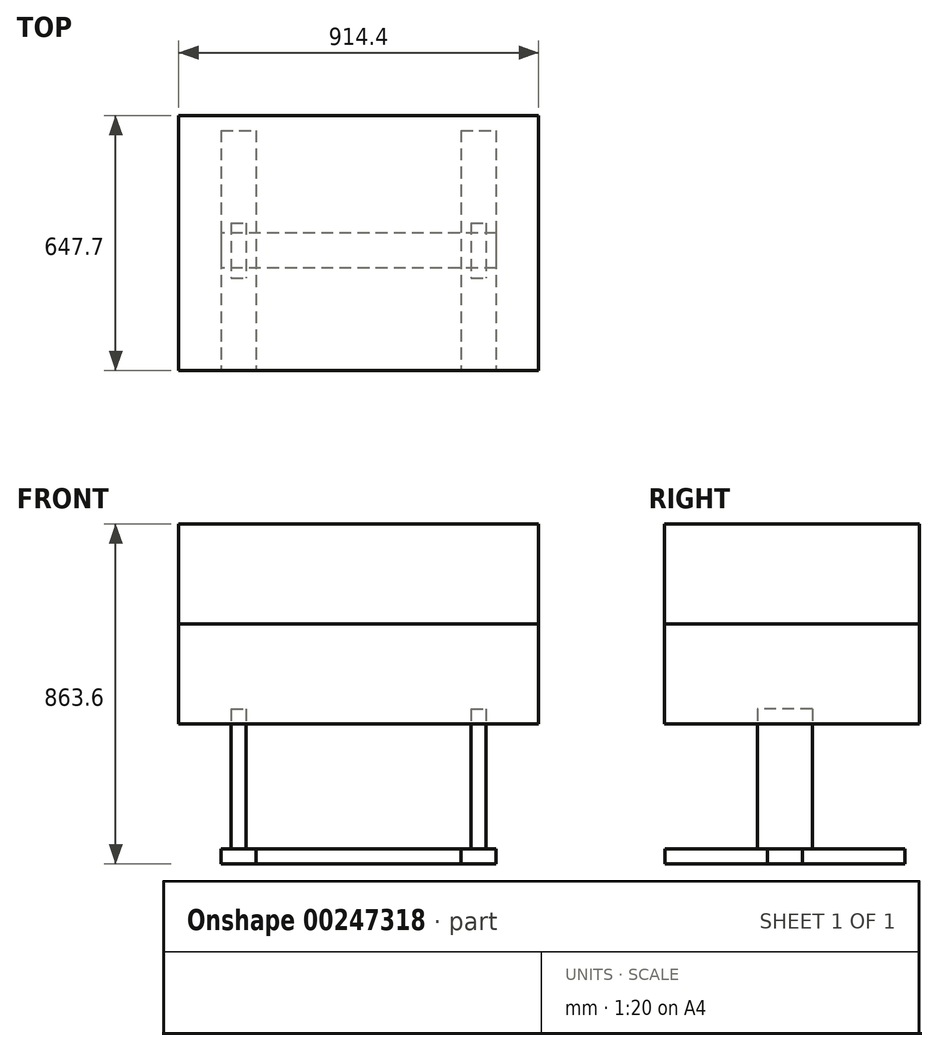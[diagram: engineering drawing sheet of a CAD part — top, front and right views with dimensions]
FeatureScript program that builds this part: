
annotation { "Feature Type Name" : "Feature", "Feature Type Description" : "" }
export const myFeature = defineFeature(function(context is Context, id is Id, definition is map)
    precondition{}
    {
        {
            var Q0;
            Q0=qCreatedBy(makeId("Top.planeOp"),FACE);
            var sketch = newSketch(context, id + "F0", { "sketchPlane" : qUnion([Q0])});
            skLineSegment(sketch, "E0.bottom", {"start": v(-85.28, 304.8) * mm, "end": v(3.62, 304.8) * mm});
            skLineSegment(sketch, "E0.top", {"start": v(-85.28, -304.8) * mm, "end": v(3.62, -304.8) * mm});
            skLineSegment(sketch, "E0.left", {"start": v(-85.28, 304.8) * mm, "end": v(-85.28, -304.8) * mm});
            skLineSegment(sketch, "E0.right", {"start": v(3.62, 304.8) * mm, "end": v(3.62, -304.8) * mm});
            skSolve(sketch);
        }
        {
            var Q0;
            Q0=makeQuery(id+"F0.imprint","IMPRINT",FACE,{"disambiguationData":[TD([[makeQuery(id+"F0.imprint","IMPRINT",EDGE,{"derivedFrom":sQuery(id+"F0.wireOp",EDGE,"E0.bottom")}),-1.0]])]});
            extrude(context, id + "F1", {"entities" : qUnion([Q0]), "depth" : 38.1 * mm});
        }
        {
            var Q0;
            Q0=makeQuery(id+"F1.opExtrude","SWEPT_BODY",BODY,{"disambiguationData":[OSD([sQuery(id+"F0.wireOp",EDGE,"E0.bottom"),sQuery(id+"F0.wireOp",EDGE,"E0.top"),sQuery(id+"F0.wireOp",EDGE,"E0.left"),sQuery(id+"F0.wireOp",EDGE,"E0.right")])]});
            transform(context, id + "F2", {"entities" : qUnion([Q0]), "transformType" : TransformType.TRANSLATION_3D, "dx" : 609.6 * mm, "dy" : 0 * mm, "dz" : 0 * mm, "makeCopy" : true});
        }
        {
            var Q0;
            Q0=makeQuery(id+"F2.opPattern","COPY",FACE,{"derivedFrom":makeQuery(id+"F1.opExtrude","SWEPT_FACE",FACE,{"disambiguationData":[OSD([sQuery(id+"F0.wireOp",EDGE,"E0.bottom")])]}),"instanceName":"1"});
            var sketch = newSketch(context, id + "F3", { "sketchPlane" : qUnion([Q0])});
            skLineSegment(sketch, "E1.bottom", {"start": v(-613.22, 38.1) * mm, "end": v(85.28, 38.1) * mm});
            skLineSegment(sketch, "E1.top", {"start": v(-613.22, 0) * mm, "end": v(85.28, 0) * mm});
            skLineSegment(sketch, "E1.left", {"start": v(-613.22, 38.1) * mm, "end": v(-613.22, 0) * mm});
            skLineSegment(sketch, "E1.right", {"start": v(85.28, 38.1) * mm, "end": v(85.28, 0) * mm});
            skSolve(sketch);
        }
        {
            var Q0;
            Q0 = qSketchRegion(id + "F3", true);
            extrude(context, id + "F4", {"entities" : qUnion([Q0]), "depth" : 88.9 * mm});
        }
        {
            var Q0;
            Q0=makeQuery(id+"F4.opExtrude","SWEPT_BODY",BODY,{"disambiguationData":[OSD([sQuery(id+"F3.wireOp",EDGE,"E1.bottom"),sQuery(id+"F3.wireOp",EDGE,"E1.top"),sQuery(id+"F3.wireOp",EDGE,"E1.left"),sQuery(id+"F3.wireOp",EDGE,"E1.right")])]});
            transform(context, id + "F5", {"entities" : qUnion([Q0]), "transformType" : TransformType.TRANSLATION_3D, "dx" : 0 * mm, "dy" : -349.25 * mm, "dz" : 0 * mm, "makeCopy" : false});
        }
        {
            var Q0;
            Q0=makeQuery(id+"F4.opExtrude","SWEPT_FACE",FACE,{"disambiguationData":[OSD([sQuery(id+"F3.wireOp",EDGE,"E1.bottom")])]});
            var sketch = newSketch(context, id + "F6", { "sketchPlane" : qUnion([Q0])});
            skLineSegment(sketch, "E2.bottom", {"start": v(-59.88, 69.85) * mm, "end": v(-21.78, 69.85) * mm});
            skLineSegment(sketch, "E2.top", {"start": v(-59.88, -69.85) * mm, "end": v(-21.78, -69.85) * mm});
            skLineSegment(sketch, "E2.left", {"start": v(-59.88, 69.85) * mm, "end": v(-59.88, -69.85) * mm});
            skLineSegment(sketch, "E2.right", {"start": v(-21.78, 69.85) * mm, "end": v(-21.78, -69.85) * mm});
            skSolve(sketch);
        }
        {
            var Q0;
            Q0 = qSketchRegion(id + "F6", true);
            extrude(context, id + "F7", {"entities" : qUnion([Q0]), "depth" : 355.6 * mm});
        }
        {
            var Q0;
            Q0=makeQuery(id+"F7.opExtrude","SWEPT_BODY",BODY,{"disambiguationData":[OSD([sQuery(id+"F6.wireOp",EDGE,"E2.bottom"),sQuery(id+"F6.wireOp",EDGE,"E2.top"),sQuery(id+"F6.wireOp",EDGE,"E2.left"),sQuery(id+"F6.wireOp",EDGE,"E2.right")])]});
            transform(context, id + "F8", {"entities" : qUnion([Q0]), "transformType" : TransformType.TRANSLATION_3D, "dx" : 609.6 * mm, "dy" : 0 * mm, "dz" : 0 * mm, "makeCopy" : true});
        }
        {
            var Q0;
            Q0=qCreatedBy(makeId("Top.planeOp"),FACE);
            var sketch = newSketch(context, id + "F9", { "sketchPlane" : qUnion([Q0])});
            skLineSegment(sketch, "E3.bottom", {"start": v(-193.23, -305.35) * mm, "end": v(721.17, -305.35) * mm});
            skLineSegment(sketch, "E3.top", {"start": v(-193.23, 342.35) * mm, "end": v(721.17, 342.35) * mm});
            skLineSegment(sketch, "E3.left", {"start": v(-193.23, -305.35) * mm, "end": v(-193.23, 342.35) * mm});
            skLineSegment(sketch, "E3.right", {"start": v(721.17, -305.35) * mm, "end": v(721.17, 342.35) * mm});
            skSolve(sketch);
        }
        {
            var Q0;
            Q0=makeQuery(id+"F9.imprint","IMPRINT",FACE,{"disambiguationData":[TD([[makeQuery(id+"F9.imprint","IMPRINT",EDGE,{"derivedFrom":sQuery(id+"F9.wireOp",EDGE,"E3.bottom")}),1.0]])]});
            extrude(context, id + "F10", {"entities" : qUnion([Q0]), "depth" : 254 * mm});
        }
        {
            var Q0;
            Q0=makeQuery(id+"F10.opExtrude","SWEPT_BODY",BODY,{"disambiguationData":[OSD([sQuery(id+"F9.wireOp",EDGE,"E3.bottom"),sQuery(id+"F9.wireOp",EDGE,"E3.top"),sQuery(id+"F9.wireOp",EDGE,"E3.left"),sQuery(id+"F9.wireOp",EDGE,"E3.right")])]});
            transform(context, id + "F11", {"entities" : qUnion([Q0]), "transformType" : TransformType.TRANSLATION_3D, "dx" : 0 * mm, "dy" : 0 * mm, "dz" : 609.6 * mm, "makeCopy" : false});
        }
        {
            var Q0;
            Q0=makeQuery(id+"F10.opExtrude","SWEPT_BODY",BODY,{"disambiguationData":[OSD([sQuery(id+"F9.wireOp",EDGE,"E3.bottom"),sQuery(id+"F9.wireOp",EDGE,"E3.top"),sQuery(id+"F9.wireOp",EDGE,"E3.left"),sQuery(id+"F9.wireOp",EDGE,"E3.right")])]});
            transform(context, id + "F12", {"entities" : qUnion([Q0]), "transformType" : TransformType.TRANSLATION_3D, "dx" : 0 * mm, "dy" : 0 * mm, "dz" : -254 * mm, "makeCopy" : true});
        }
    });
